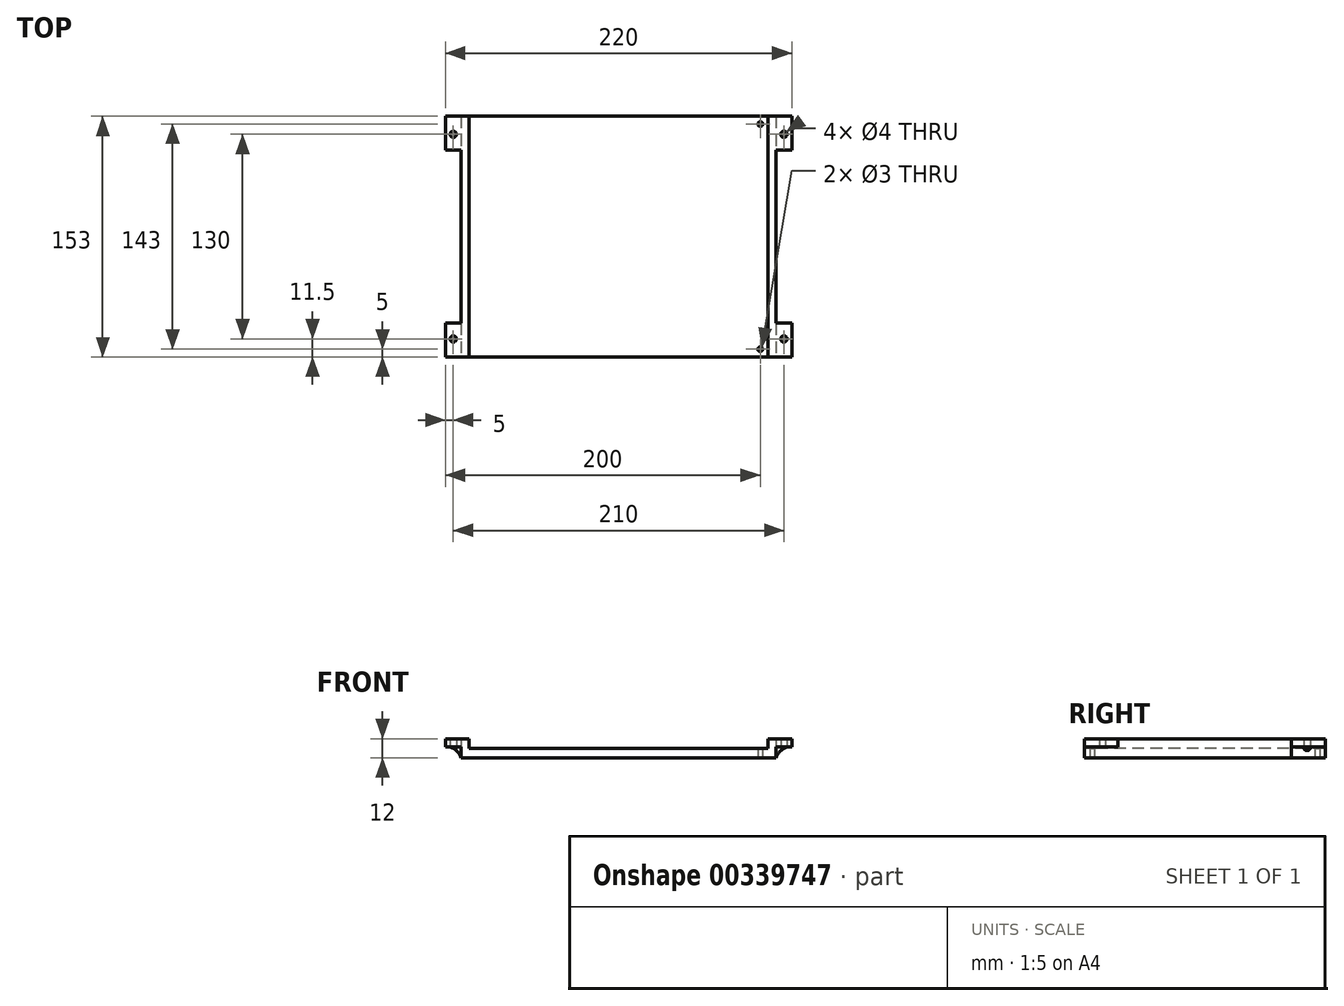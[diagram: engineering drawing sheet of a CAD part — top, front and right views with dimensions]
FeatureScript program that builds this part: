
annotation { "Feature Type Name" : "Feature", "Feature Type Description" : "" }
export const myFeature = defineFeature(function(context is Context, id is Id, definition is map)
    precondition{}
    {
        {
            var Q0;
            Q0=qCreatedBy(makeId("Top.planeOp"),FACE);
            var sketch = newSketch(context, id + "F0", { "sketchPlane" : qUnion([Q0])});
            skLineSegment(sketch, "E0.bottom", {"start": v(0, 0) * mm, "end": v(200, 0) * mm});
            skLineSegment(sketch, "E0.top", {"start": v(0, -153) * mm, "end": v(200, -153) * mm});
            skLineSegment(sketch, "E0.left", {"start": v(0, 0) * mm, "end": v(0, -153) * mm});
            skLineSegment(sketch, "E0.right", {"start": v(200, 0) * mm, "end": v(200, -153) * mm});
            skLineSegment(sketch, "E1", {"start": v(190, -153) * mm, "end": v(190, -148) * mm});
            skLineSegment(sketch, "E2", {"start": v(190, -148) * mm, "end": v(200, -148) * mm});
            skLineSegment(sketch, "E3", {"start": v(200, -5) * mm, "end": v(190, -5) * mm});
            skLineSegment(sketch, "E4", {"start": v(190, -5) * mm, "end": v(190, 0) * mm});
            skCircle(sketch, "E5", {"center": v(190, -148) * mm, "radius": 1.5 * mm});
            skCircle(sketch, "E6", {"center": v(190, -5) * mm, "radius": 1.5 * mm});
            skSolve(sketch);
        }
        {
            var Q0;
            Q0=makeQuery(id+"F0.imprint","IMPRINT",FACE,{"disambiguationData":[TD([[makeQuery(id+"F0.imprint","IMPRINT",EDGE,{"derivedFrom":sQuery(id+"F0.wireOp",EDGE,"E0.bottom")}),-1.0]])]});
            var Q1;
            {var subQ18=sQuery(id+"F0.wireOp",EDGE,"E0.left");Q1=makeQuery(id+"F0.imprint","IMPRINT",FACE,{"disambiguationData":[TD([[makeQuery(id+"F0.imprint","IMPRINT",EDGE,{"derivedFrom":subQ18}),1.0]])]});}
            var Q2;
            {var subQ1=sQuery(id+"F0.wireOp",EDGE,"E0.top");var subQ5=sQuery(id+"F0.wireOp",EDGE,"E0.right");var subQ6=makeQuery(id+"F0.imprint","INTERSECT",VERTEX,{"derivedFrom":[subQ1,subQ5]});Q2=makeQuery(id+"F0.imprint","IMPRINT",FACE,{"disambiguationData":[TD([[makeQuery(id+"F0.imprint","IMPRINT",EDGE,{"disambiguationData":[TD([[subQ6,1.0]])],"derivedFrom":subQ1}),1.0]])]});}
            extrude(context, id + "F1", {"entities" : qUnion([Q0, Q1, Q2]), "depth" : 6 * mm});
        }
        {
            var Q0;
            Q0=makeQuery(id+"F1.opExtrude","CAP_FACE",FACE,{"disambiguationData":[OSD([sQuery(id+"F0.wireOp",EDGE,"E0.bottom"),sQuery(id+"F0.wireOp",EDGE,"E0.top"),sQuery(id+"F0.wireOp",EDGE,"E0.left"),sQuery(id+"F0.wireOp",EDGE,"E0.right")])],"isStart":false});
            var sketch = newSketch(context, id + "F2", { "sketchPlane" : qUnion([Q0])});
            skLineSegment(sketch, "E7.bottom", {"start": v(0, 0) * mm, "end": v(5, 0) * mm});
            skLineSegment(sketch, "E7.top", {"start": v(0, -153) * mm, "end": v(5, -153) * mm});
            skLineSegment(sketch, "E7.left", {"start": v(0, 0) * mm, "end": v(0, -153) * mm});
            skLineSegment(sketch, "E7.right", {"start": v(5, 0) * mm, "end": v(5, -153) * mm});
            skLineSegment(sketch, "E8.bottom", {"start": v(200, 0) * mm, "end": v(195, 0) * mm});
            skLineSegment(sketch, "E8.top", {"start": v(200, -153) * mm, "end": v(195, -153) * mm});
            skLineSegment(sketch, "E8.left", {"start": v(200, 0) * mm, "end": v(200, -153) * mm});
            skLineSegment(sketch, "E8.right", {"start": v(195, 0) * mm, "end": v(195, -153) * mm});
            skSolve(sketch);
        }
        {
            var Q0;
            Q0=makeQuery(id+"F2.imprint","IMPRINT",FACE,{"disambiguationData":[TD([[makeQuery(id+"F2.imprint","IMPRINT",EDGE,{"derivedFrom":sQuery(id+"F2.wireOp",EDGE,"E7.bottom")}),-1.0]])]});
            var Q1;
            Q1=makeQuery(id+"F2.imprint","IMPRINT",FACE,{"disambiguationData":[TD([[makeQuery(id+"F2.imprint","IMPRINT",EDGE,{"derivedFrom":sQuery(id+"F2.wireOp",EDGE,"E8.bottom")}),-1.0]])]});
            extrude(context, id + "F3", {"entities" : qUnion([Q0, Q1]), "operationType" : NewBodyOperationType.ADD, "depth" : 1 * mm});
        }
        {
            var Q0;
            Q0=makeQuery(id+"F3.opExtrude","CAP_FACE",FACE,{"disambiguationData":[OSD([sQuery(id+"F2.wireOp",EDGE,"E7.bottom"),sQuery(id+"F2.wireOp",EDGE,"E7.top"),sQuery(id+"F2.wireOp",EDGE,"E7.left"),sQuery(id+"F2.wireOp",EDGE,"E7.right")])],"isStart":false});
            var sketch = newSketch(context, id + "F4", { "sketchPlane" : qUnion([Q0])});
            skPoint(sketch, "E9.oppositeSnap0", {"position": v(2.5, 0) * mm});
            skLineSegment(sketch, "E9.bottom", {"start": v(5, -153) * mm, "end": v(-10, -153) * mm});
            skLineSegment(sketch, "E9.top", {"start": v(5, 0) * mm, "end": v(-10, 0) * mm});
            skLineSegment(sketch, "E9.left", {"start": v(5, -153) * mm, "end": v(5, 0) * mm});
            skLineSegment(sketch, "E10.bottom", {"start": v(195, -153) * mm, "end": v(210, -153) * mm});
            skLineSegment(sketch, "E10.top", {"start": v(195, 0) * mm, "end": v(210, 0) * mm});
            skLineSegment(sketch, "E10.left", {"start": v(195, -153) * mm, "end": v(195, 0) * mm});
            skLineSegment(sketch, "E10.right", {"start": v(210, -153) * mm, "end": v(210, 0) * mm});
            skLineSegment(sketch, "E11", {"start": v(205, -153) * mm, "end": v(205, 0) * mm});
            skLineSegment(sketch, "E12", {"start": v(-5, -153) * mm, "end": v(-5, 0) * mm});
            skCircle(sketch, "E13", {"center": v(-5, -141.5) * mm, "radius": 2 * mm});
            skCircle(sketch, "E14", {"center": v(-5, -11.5) * mm, "radius": 2 * mm});
            skCircle(sketch, "E15", {"center": v(205, -11.5) * mm, "radius": 2 * mm});
            skCircle(sketch, "E16", {"center": v(205, -141.5) * mm, "radius": 2 * mm});
            skLineSegment(sketch, "E17", {"start": v(205, -141.5) * mm, "end": v(205, -76.5) * mm});
            skLineSegment(sketch, "E18", {"start": v(205, -76.5) * mm, "end": v(205, -11.5) * mm});
            skLineSegment(sketch, "E19", {"start": v(-5, -141.5) * mm, "end": v(-5, -76.5) * mm});
            skLineSegment(sketch, "E20", {"start": v(-5, -76.5) * mm, "end": v(-5, -11.5) * mm});
            skLineSegment(sketch, "E21", {"start": v(-10, -21.5) * mm, "end": v(0, -21.5) * mm});
            skLineSegment(sketch, "E22", {"start": v(195, -131.5) * mm, "end": v(210, -131.5) * mm});
            skLineSegment(sketch, "E23", {"start": v(210, -21.5) * mm, "end": v(195, -21.5) * mm});
            skLineSegment(sketch, "E24", {"start": v(200, -21.5) * mm, "end": v(200, -131.5) * mm});
            skLineSegment(sketch, "E25", {"start": v(-10, 0) * mm, "end": v(-10, -153) * mm});
            skLineSegment(sketch, "E26", {"start": v(0, -131.5) * mm, "end": v(-10, -131.5) * mm});
            skSolve(sketch);
        }
        {
            var Q0;
            {var subQ2=sQuery(id+"F4.wireOp",EDGE,"E9.left");Q0=makeQuery(id+"F4.imprint","IMPRINT",FACE,{"disambiguationData":[TD([[makeQuery(id+"F4.imprint","IMPRINT",EDGE,{"derivedFrom":subQ2}),-1.0]])]});}
            var Q1;
            {var subQ5=sQuery(id+"F4.wireOp",EDGE,"E10.left");var subQ6=sQuery(id+"F4.wireOp",EDGE,"E10.bottom");var subQ7=makeQuery(id+"F4.imprint","INTERSECT",VERTEX,{"derivedFrom":[subQ6,subQ5]});Q1=makeQuery(id+"F4.imprint","IMPRINT",FACE,{"disambiguationData":[TD([[makeQuery(id+"F4.imprint","IMPRINT",EDGE,{"disambiguationData":[TD([[subQ7,-1.0]])],"derivedFrom":subQ6}),1.0]])]});}
            var Q2;
            {var subQ5=sQuery(id+"F4.wireOp",EDGE,"E10.bottom");var subQ8=sQuery(id+"F4.wireOp",EDGE,"E10.right");var subQ11=makeQuery(id+"F4.imprint","INTERSECT",VERTEX,{"derivedFrom":[subQ5,subQ8]});Q2=makeQuery(id+"F4.imprint","IMPRINT",FACE,{"disambiguationData":[TD([[makeQuery(id+"F4.imprint","IMPRINT",EDGE,{"disambiguationData":[TD([[subQ11,1.0]])],"derivedFrom":subQ5}),1.0]])]});}
            var Q3;
            {var subQ1=sQuery(id+"F4.wireOp",EDGE,"E10.top");var subQ5=sQuery(id+"F4.wireOp",EDGE,"E10.left");var subQ6=makeQuery(id+"F4.imprint","INTERSECT",VERTEX,{"derivedFrom":[subQ1,subQ5]});Q3=makeQuery(id+"F4.imprint","IMPRINT",FACE,{"disambiguationData":[TD([[makeQuery(id+"F4.imprint","IMPRINT",EDGE,{"disambiguationData":[TD([[subQ6,-1.0]])],"derivedFrom":subQ1}),-1.0]])]});}
            var Q4;
            {var subQ0=sQuery(id+"F4.wireOp",EDGE,"E10.right");var subQ1=sQuery(id+"F4.wireOp",EDGE,"E10.top");var subQ2=makeQuery(id+"F4.imprint","INTERSECT",VERTEX,{"derivedFrom":[subQ1,subQ0]});Q4=makeQuery(id+"F4.imprint","IMPRINT",FACE,{"disambiguationData":[TD([[makeQuery(id+"F4.imprint","IMPRINT",EDGE,{"disambiguationData":[TD([[subQ2,1.0]])],"derivedFrom":subQ1}),-1.0]])]});}
            var Q5;
            {var subQ6=sQuery(id+"F4.wireOp",EDGE,"E9.right");var subQ9=sQuery(id+"F4.wireOp",EDGE,"E9.bottom");var subQ11=makeQuery(id+"F4.imprint","INTERSECT",VERTEX,{"derivedFrom":[subQ9,subQ6]});Q5=makeQuery(id+"F4.imprint","IMPRINT",FACE,{"disambiguationData":[TD([[makeQuery(id+"F4.imprint","IMPRINT",EDGE,{"disambiguationData":[TD([[subQ11,1.0]])],"derivedFrom":subQ9}),-1.0]])]});}
            var Q6;
            {var subQ5=sQuery(id+"F4.wireOp",EDGE,"E12");var subQ9=sQuery(id+"F4.wireOp",EDGE,"E9.bottom");var subQ10=makeQuery(id+"F4.imprint","INTERSECT",VERTEX,{"derivedFrom":[subQ9,subQ5]});Q6=makeQuery(id+"F4.imprint","IMPRINT",FACE,{"disambiguationData":[TD([[makeQuery(id+"F4.imprint","IMPRINT",EDGE,{"disambiguationData":[TD([[subQ10,1.0]])],"derivedFrom":subQ9}),-1.0]])]});}
            var Q7;
            {var subQ1=sQuery(id+"F4.wireOp",EDGE,"E9.top");var subQ5=sQuery(id+"F4.wireOp",EDGE,"E9.right");var subQ6=makeQuery(id+"F4.imprint","INTERSECT",VERTEX,{"derivedFrom":[subQ1,subQ5]});Q7=makeQuery(id+"F4.imprint","IMPRINT",FACE,{"disambiguationData":[TD([[makeQuery(id+"F4.imprint","IMPRINT",EDGE,{"disambiguationData":[TD([[subQ6,1.0]])],"derivedFrom":subQ1}),1.0]])]});}
            var Q8;
            {var subQ5=sQuery(id+"F4.wireOp",EDGE,"E12");var subQ7=sQuery(id+"F4.wireOp",EDGE,"E9.top");var subQ8=makeQuery(id+"F4.imprint","INTERSECT",VERTEX,{"derivedFrom":[subQ7,subQ5]});Q8=makeQuery(id+"F4.imprint","IMPRINT",FACE,{"disambiguationData":[TD([[makeQuery(id+"F4.imprint","IMPRINT",EDGE,{"disambiguationData":[TD([[subQ8,1.0]])],"derivedFrom":subQ7}),1.0]])]});}
            var Q9;
            {var subQ5=sQuery(id+"F4.wireOp",EDGE,"E24");Q9=makeQuery(id+"F4.imprint","IMPRINT",FACE,{"disambiguationData":[TD([[makeQuery(id+"F4.imprint","IMPRINT",EDGE,{"derivedFrom":subQ5}),-1.0]])]});}
            extrude(context, id + "F5", {"entities" : qUnion([Q0, Q1, Q2, Q3, Q4, Q5, Q6, Q7, Q8, Q9]), "operationType" : NewBodyOperationType.ADD, "depth" : 5 * mm});
        }
        {
            var Q0;
            {var subQ1=sQuery(id+"F2.wireOp",EDGE,"E8.left");Q0=makeQuery(id+"F5.boolean.opBoolean","SPLIT",EDGE,{"disambiguationData":[TD([makeQuery(id+"F1.opExtrude","SWEPT_FACE",FACE,{"disambiguationData":[OSD([sQuery(id+"F0.wireOp",EDGE,"E0.top")])]})])],"derivedFrom":makeQuery(id+"F3.opExtrude","CAP_EDGE",EDGE,{"disambiguationData":[OSD([subQ1])],"isStart":false})});}
            var Q1;
            {var subQ3=sQuery(id+"F2.wireOp",EDGE,"E8.left");Q1=makeQuery(id+"F5.boolean.opBoolean","SPLIT",EDGE,{"disambiguationData":[TD([makeQuery(id+"F1.opExtrude","SWEPT_FACE",FACE,{"disambiguationData":[OSD([sQuery(id+"F0.wireOp",EDGE,"E0.bottom")])]})])],"derivedFrom":makeQuery(id+"F3.opExtrude","CAP_EDGE",EDGE,{"disambiguationData":[OSD([subQ3])],"isStart":false})});}
            var Q2;
            {var subQ0=sQuery(id+"F2.wireOp",EDGE,"E7.left");Q2=makeQuery(id+"F5.boolean.opBoolean","SPLIT",EDGE,{"disambiguationData":[TD([makeQuery(id+"F1.opExtrude","SWEPT_FACE",FACE,{"disambiguationData":[OSD([sQuery(id+"F0.wireOp",EDGE,"E0.bottom")])]})])],"derivedFrom":makeQuery(id+"F3.opExtrude","CAP_EDGE",EDGE,{"disambiguationData":[OSD([subQ0])],"isStart":false})});}
            var Q3;
            {var subQ0=sQuery(id+"F2.wireOp",EDGE,"E7.left");Q3=makeQuery(id+"F5.boolean.opBoolean","SPLIT",EDGE,{"disambiguationData":[TD([makeQuery(id+"F1.opExtrude","SWEPT_FACE",FACE,{"disambiguationData":[OSD([sQuery(id+"F0.wireOp",EDGE,"E0.top")])]})])],"derivedFrom":makeQuery(id+"F3.opExtrude","CAP_EDGE",EDGE,{"disambiguationData":[OSD([subQ0])],"isStart":false})});}
            fillet(context, id + "F6", {"entities" : qUnion([Q0, Q1, Q2, Q3]), "radius" : 10 * mm, "tangentPropagation" : true, "allowEdgeOverflow" : false});
        }
    });
